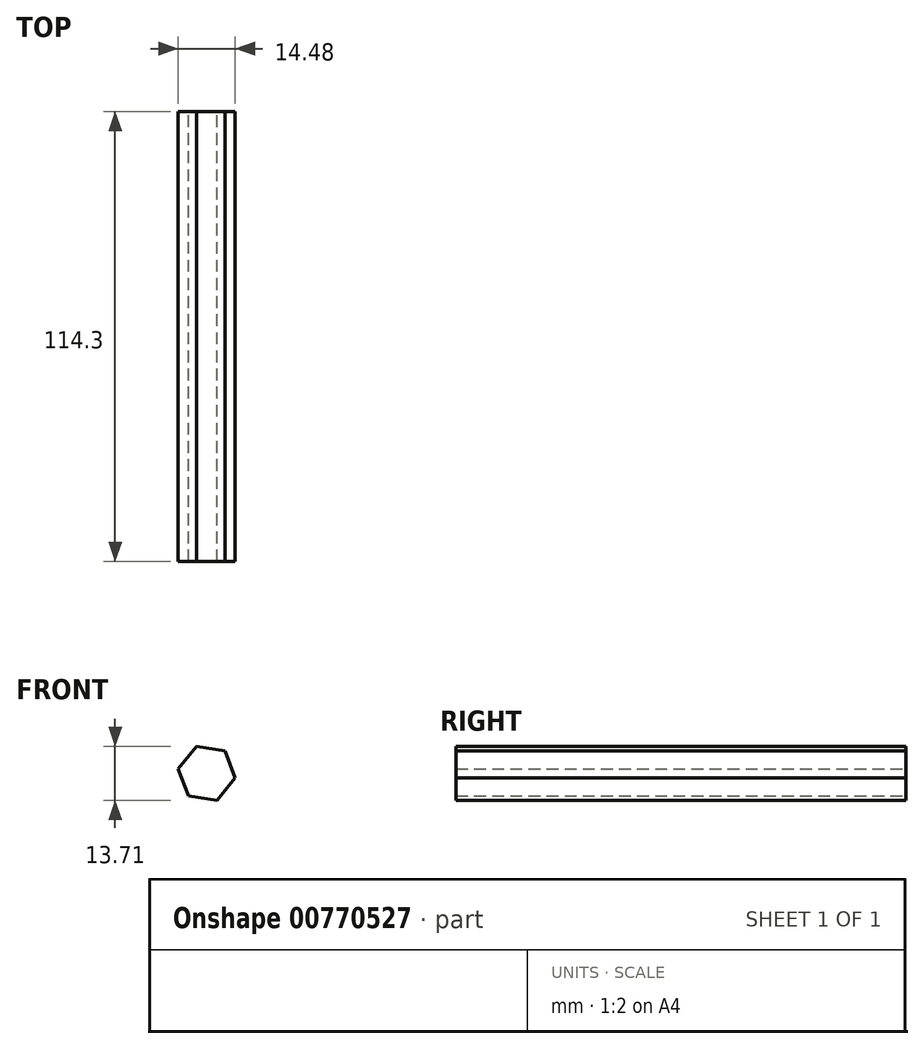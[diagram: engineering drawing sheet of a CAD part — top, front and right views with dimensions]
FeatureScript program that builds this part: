
annotation { "Feature Type Name" : "Feature", "Feature Type Description" : "" }
export const myFeature = defineFeature(function(context is Context, id is Id, definition is map)
    precondition{}
    {
        {
            var Q0;
            Q0=qCreatedBy(makeId("Front.planeOp"),FACE);
            var sketch = newSketch(context, id + "F0", { "sketchPlane" : qUnion([Q0])});
            skCircle(sketch, "E0.cCircle", {"center": v(-13.37, 22.26) * mm, "radius": 6.35 * mm, "construction": true});
            skLineSegment(sketch, "E0.0", {"start": v(-6.13, 21.09) * mm, "end": v(-10.76, 15.4) * mm});
            skLineSegment(sketch, "E0.1", {"start": v(-10.76, 15.4) * mm, "end": v(-18, 16.57) * mm});
            skLineSegment(sketch, "E0.2", {"start": v(-18, 16.57) * mm, "end": v(-20.6, 23.43) * mm});
            skLineSegment(sketch, "E0.3", {"start": v(-20.6, 23.43) * mm, "end": v(-15.98, 29.1) * mm});
            skLineSegment(sketch, "E0.4", {"start": v(-15.98, 29.1) * mm, "end": v(-8.74, 27.94) * mm});
            skLineSegment(sketch, "E0.5", {"start": v(-8.74, 27.94) * mm, "end": v(-6.13, 21.09) * mm});
            skPoint(sketch, "E0.0.midPoint", {"position": v(-8.45, 18.25) * mm});
            skSolve(sketch);
        }
        {
            var Q0;
            Q0=makeQuery(id+"F0.imprint","IMPRINT",FACE,{"disambiguationData":[TD([[makeQuery(id+"F0.imprint","IMPRINT",EDGE,{"derivedFrom":sQuery(id+"F0.wireOp",EDGE,"E0.0")}),-1.0]])]});
            extrude(context, id + "F1", {"entities" : qUnion([Q0]), "depth" : 114.3 * mm, "offsetDistance" : 25.4 * mm});
        }
    });
